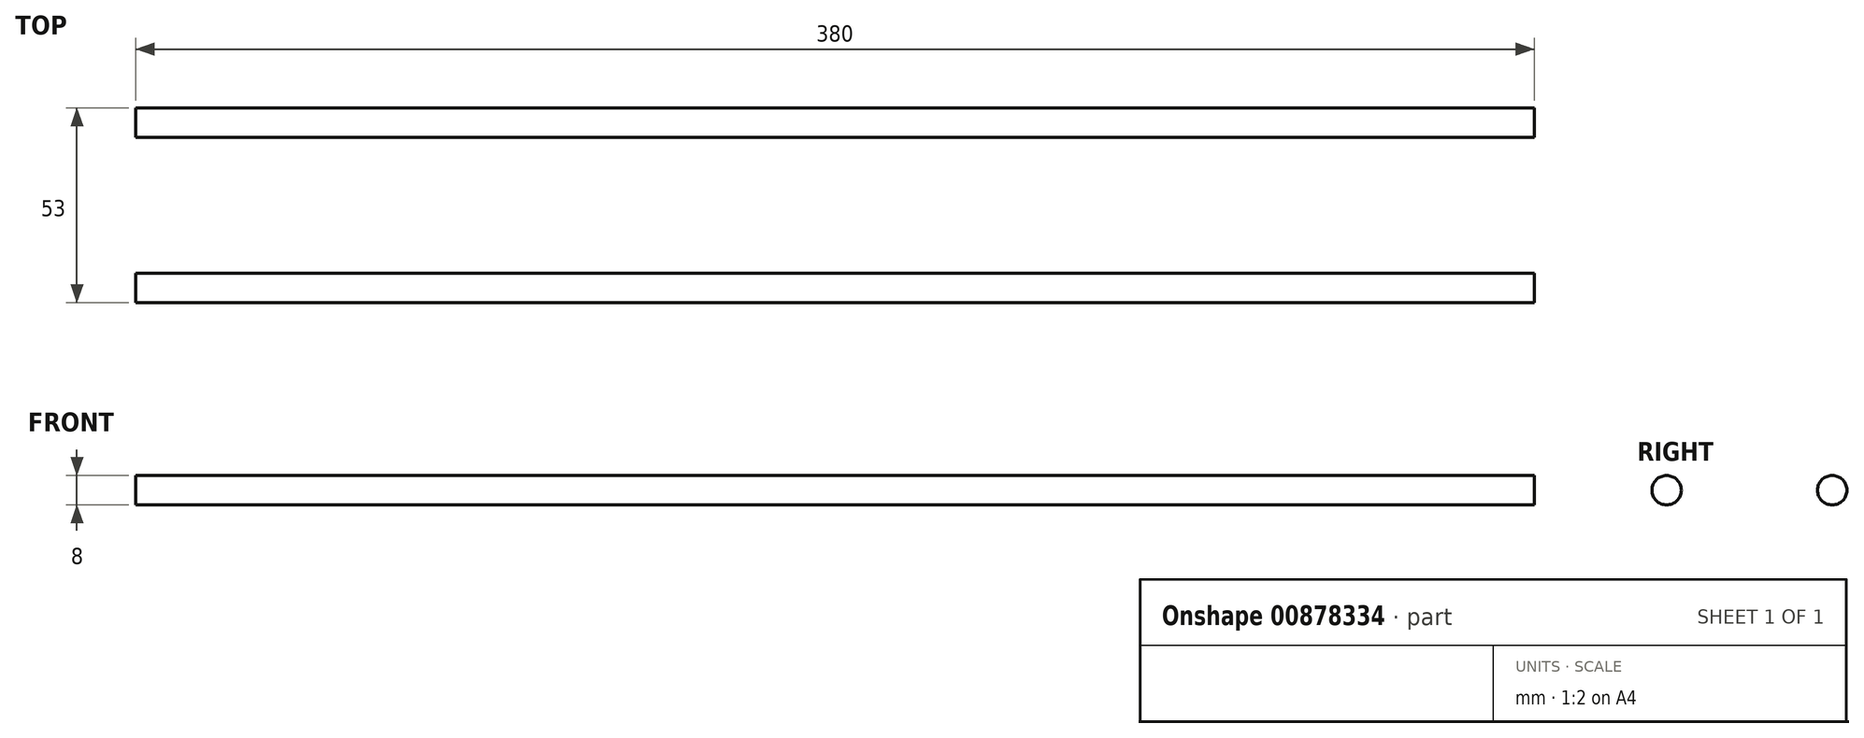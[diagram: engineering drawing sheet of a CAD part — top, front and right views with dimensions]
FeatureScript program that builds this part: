
annotation { "Feature Type Name" : "Feature", "Feature Type Description" : "" }
export const myFeature = defineFeature(function(context is Context, id is Id, definition is map)
    precondition{}
    {
        {
            var Q0;
            Q0=qCreatedBy(makeId("Right.planeOp"),FACE);
            var sketch = newSketch(context, id + "F0", { "sketchPlane" : qUnion([Q0])});
            skCircle(sketch, "E0", {"center": v(0, 0) * mm, "radius": 4 * mm});
            skCircle(sketch, "E1", {"center": v(45, 0) * mm, "radius": 4 * mm});
            skSolve(sketch);
        }
        {
            var Q0;
            Q0=makeQuery(id+"F0.imprint","IMPRINT",FACE,{"disambiguationData":[TD([[makeQuery(id+"F0.imprint","IMPRINT",EDGE,{"derivedFrom":sQuery(id+"F0.wireOp",EDGE,"E0")}),1.0]])]});
            var Q1;
            Q1=makeQuery(id+"F0.imprint","IMPRINT",FACE,{"disambiguationData":[TD([[makeQuery(id+"F0.imprint","IMPRINT",EDGE,{"derivedFrom":sQuery(id+"F0.wireOp",EDGE,"E1")}),1.0]])]});
            extrude(context, id + "F1", {"entities" : qUnion([Q0, Q1]), "depth" : 380 * mm, "offsetDistance" : 25 * mm});
        }
    });
